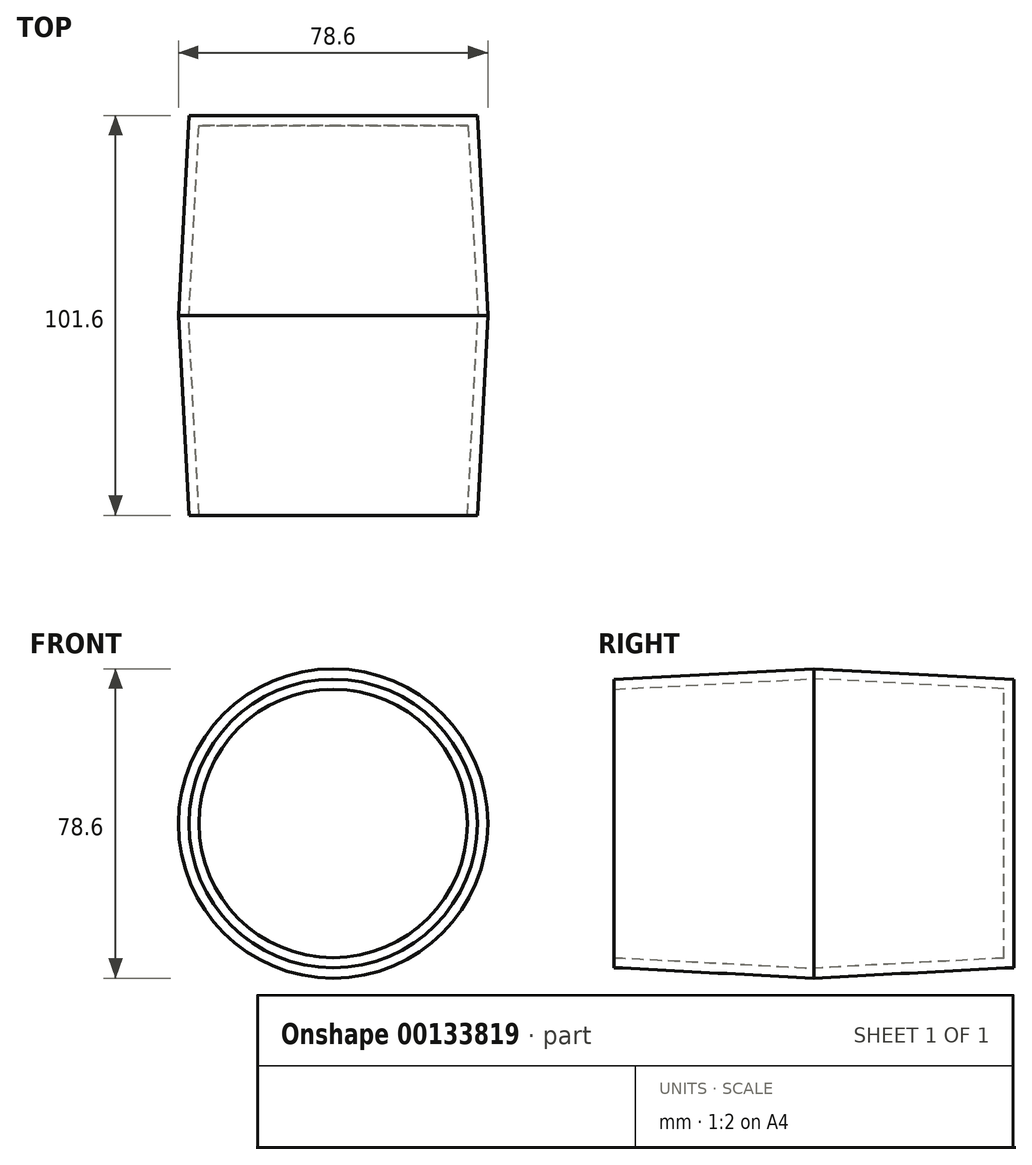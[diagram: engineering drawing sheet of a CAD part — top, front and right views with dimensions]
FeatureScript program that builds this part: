
annotation { "Feature Type Name" : "Feature", "Feature Type Description" : "" }
export const myFeature = defineFeature(function(context is Context, id is Id, definition is map)
    precondition{}
    {
        {
            var Q0;
            Q0=qCreatedBy(makeId("Front.planeOp"),FACE);
            var sketch = newSketch(context, id + "F0", { "sketchPlane" : qUnion([Q0])});
            skCircle(sketch, "E0", {"center": v(0, 0) * mm, "radius": 39.3 * mm});
            skSolve(sketch);
        }
        {
            var Q0;
            Q0 = qSketchRegion(id + "F0", true);
            extrude(context, id + "F1", {"entities" : qUnion([Q0]), "endBound" : BoundingType.SYMMETRIC, "depth" : 101.6 * mm, "hasDraft" : true, "draftAngle" : 3 * degree, "draftPullDirection" : true});
        }
        {
            var Q0;
            Q0=makeQuery(id+"F1.opExtrude","CAP_FACE",FACE,{"disambiguationData":[OSD([sQuery(id+"F0.wireOp",EDGE,"E0")])],"isStart":false});
            shell(context, id + "F2", {"entities" : qUnion([Q0]), "thickness" : 2.54 * mm});
        }
    });
